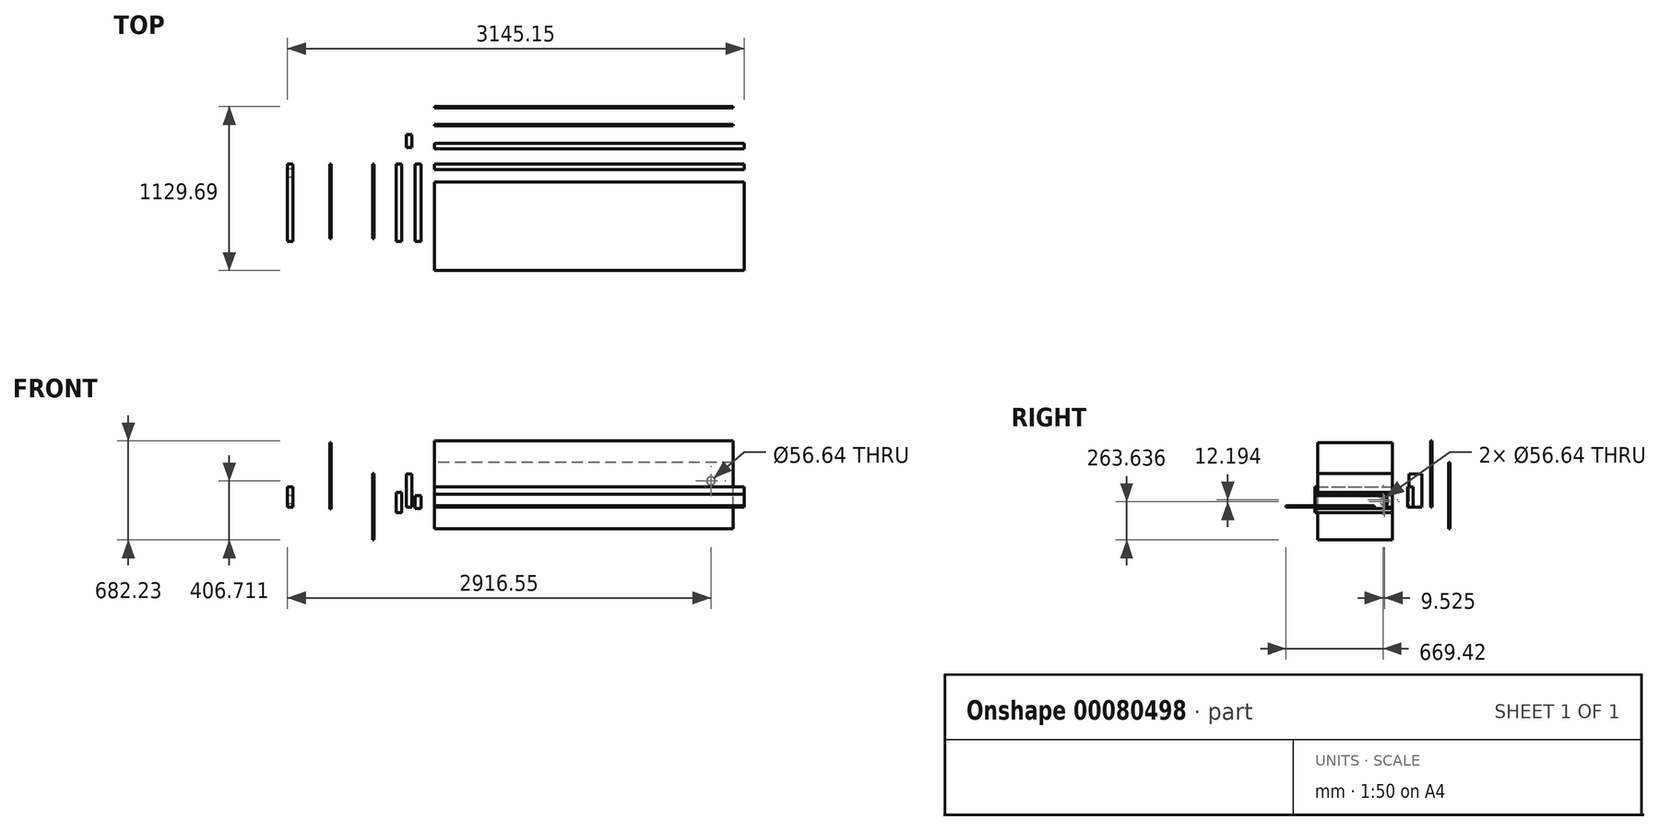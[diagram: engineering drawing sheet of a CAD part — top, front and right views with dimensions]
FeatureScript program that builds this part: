
annotation { "Feature Type Name" : "Feature", "Feature Type Description" : "" }
export const myFeature = defineFeature(function(context is Context, id is Id, definition is map)
    precondition{}
    {
        {
            var Q0;
            Q0=qCreatedBy(makeId("Right.planeOp"),FACE);
            var sketch = newSketch(context, id + "F0", { "sketchPlane" : qUnion([Q0])});
            skLineSegment(sketch, "E0.bottom", {"start": v(0, 0) * mm, "end": v(-38.1, 0) * mm});
            skLineSegment(sketch, "E0.top", {"start": v(0, 88.9) * mm, "end": v(-38.1, 88.9) * mm});
            skLineSegment(sketch, "E0.left", {"start": v(0, 0) * mm, "end": v(0, 88.9) * mm});
            skLineSegment(sketch, "E0.right", {"start": v(-38.1, 0) * mm, "end": v(-38.1, 88.9) * mm});
            skSolve(sketch);
        }
        {
            var Q0;
            Q0=makeQuery(id+"F0.imprint","IMPRINT",FACE,{"disambiguationData":[TD([[makeQuery(id+"F0.imprint","IMPRINT",EDGE,{"derivedFrom":sQuery(id+"F0.wireOp",EDGE,"E0.bottom")}),-1.0]])]});
            extrude(context, id + "F1", {"entities" : qUnion([Q0]), "depth" : 2133.6 * mm});
        }
        {
            var Q0;
            Q0=qCreatedBy(makeId("Front.planeOp"),FACE);
            var sketch = newSketch(context, id + "F2", { "sketchPlane" : qUnion([Q0])});
            skLineSegment(sketch, "E1.bottom", {"start": v(-92.86, -7.97) * mm, "end": v(-130.96, -7.97) * mm});
            skLineSegment(sketch, "E1.top", {"start": v(-92.86, 80.93) * mm, "end": v(-130.96, 80.93) * mm});
            skLineSegment(sketch, "E1.left", {"start": v(-92.86, -7.97) * mm, "end": v(-92.86, 80.93) * mm});
            skLineSegment(sketch, "E1.right", {"start": v(-130.96, -7.97) * mm, "end": v(-130.96, 80.93) * mm});
            skSolve(sketch);
        }
        {
            var Q0;
            Q0=makeQuery(id+"F2.imprint","IMPRINT",FACE,{"disambiguationData":[TD([[makeQuery(id+"F2.imprint","IMPRINT",EDGE,{"derivedFrom":sQuery(id+"F2.wireOp",EDGE,"E1.bottom")}),-1.0]])]});
            extrude(context, id + "F3", {"entities" : qUnion([Q0]), "depth" : 533.4 * mm});
        }
        {
            var Q0;
            Q0=qCreatedBy(makeId("Right.planeOp"),FACE);
            var sketch = newSketch(context, id + "F4", { "sketchPlane" : qUnion([Q0])});
            skLineSegment(sketch, "E2.bottom", {"start": v(105.82, 0) * mm, "end": v(143.92, 0) * mm});
            skLineSegment(sketch, "E2.top", {"start": v(105.82, 139.7) * mm, "end": v(143.92, 139.7) * mm});
            skLineSegment(sketch, "E2.left", {"start": v(105.82, 0) * mm, "end": v(105.82, 139.7) * mm});
            skLineSegment(sketch, "E2.right", {"start": v(143.92, 0) * mm, "end": v(143.92, 139.7) * mm});
            skSolve(sketch);
        }
        {
            var Q0;
            Q0=makeQuery(id+"F4.imprint","IMPRINT",FACE,{"disambiguationData":[TD([[makeQuery(id+"F4.imprint","IMPRINT",EDGE,{"derivedFrom":sQuery(id+"F4.wireOp",EDGE,"E2.bottom")}),1.0]])]});
            extrude(context, id + "F5", {"entities" : qUnion([Q0]), "depth" : 2133.6 * mm});
        }
        {
            var Q0;
            Q0=qCreatedBy(makeId("Front.planeOp"),FACE);
            var sketch = newSketch(context, id + "F6", { "sketchPlane" : qUnion([Q0])});
            skLineSegment(sketch, "E3.bottom", {"start": v(-225.29, -37.86) * mm, "end": v(-263.39, -37.86) * mm});
            skLineSegment(sketch, "E3.top", {"start": v(-225.29, 101.84) * mm, "end": v(-263.39, 101.84) * mm});
            skLineSegment(sketch, "E3.left", {"start": v(-225.29, -37.86) * mm, "end": v(-225.29, 101.84) * mm});
            skLineSegment(sketch, "E3.right", {"start": v(-263.39, -37.86) * mm, "end": v(-263.39, 101.84) * mm});
            skSolve(sketch);
        }
        {
            var Q0;
            Q0=makeQuery(id+"F6.imprint","IMPRINT",FACE,{"disambiguationData":[TD([[makeQuery(id+"F6.imprint","IMPRINT",EDGE,{"derivedFrom":sQuery(id+"F6.wireOp",EDGE,"E3.bottom")}),-1.0]])]});
            extrude(context, id + "F7", {"entities" : qUnion([Q0]), "depth" : 533.4 * mm});
        }
        {
            var Q0;
            Q0=qCreatedBy(makeId("Top.planeOp"),FACE);
            var sketch = newSketch(context, id + "F8", { "sketchPlane" : qUnion([Q0])});
            skLineSegment(sketch, "E4.bottom", {"start": v(-155.43, 116.63) * mm, "end": v(-193.53, 116.63) * mm});
            skLineSegment(sketch, "E4.top", {"start": v(-155.43, 205.53) * mm, "end": v(-193.53, 205.53) * mm});
            skLineSegment(sketch, "E4.left", {"start": v(-155.43, 116.63) * mm, "end": v(-155.43, 205.53) * mm});
            skLineSegment(sketch, "E4.right", {"start": v(-193.53, 116.63) * mm, "end": v(-193.53, 205.53) * mm});
            skSolve(sketch);
        }
        {
            var Q0;
            Q0=makeQuery(id+"F8.imprint","IMPRINT",FACE,{"disambiguationData":[TD([[makeQuery(id+"F8.imprint","IMPRINT",EDGE,{"derivedFrom":sQuery(id+"F8.wireOp",EDGE,"E4.bottom")}),-1.0]])]});
            extrude(context, id + "F9", {"entities" : qUnion([Q0]), "depth" : 228.6 * mm});
        }
        {
            var Q0;
            Q0=qCreatedBy(makeId("Top.planeOp"),FACE);
            var sketch = newSketch(context, id + "F10", { "sketchPlane" : qUnion([Q0])});
            skLineSegment(sketch, "E5.bottom", {"start": v(0, -123.32) * mm, "end": v(2133.6, -123.32) * mm});
            skLineSegment(sketch, "E5.top", {"start": v(0, -732.92) * mm, "end": v(2133.6, -732.92) * mm});
            skLineSegment(sketch, "E5.left", {"start": v(0, -123.32) * mm, "end": v(0, -732.92) * mm});
            skLineSegment(sketch, "E5.right", {"start": v(2133.6, -123.32) * mm, "end": v(2133.6, -732.92) * mm});
            skSolve(sketch);
        }
        {
            var Q0;
            Q0=makeQuery(id+"F10.imprint","IMPRINT",FACE,{"disambiguationData":[TD([[makeQuery(id+"F10.imprint","IMPRINT",EDGE,{"derivedFrom":sQuery(id+"F10.wireOp",EDGE,"E5.bottom")}),-1.0]])]});
            extrude(context, id + "F11", {"entities" : qUnion([Q0]), "depth" : 9.52 * mm});
        }
        {
            var Q0;
            Q0=qCreatedBy(makeId("Right.planeOp"),FACE);
            var sketch = newSketch(context, id + "F12", { "sketchPlane" : qUnion([Q0])});
            skLineSegment(sketch, "E6.bottom", {"start": v(263.25, 0) * mm, "end": v(272.78, 0) * mm});
            skLineSegment(sketch, "E6.top", {"start": v(263.25, 457.2) * mm, "end": v(272.78, 457.2) * mm});
            skLineSegment(sketch, "E6.left", {"start": v(263.25, 0) * mm, "end": v(263.25, 457.2) * mm});
            skLineSegment(sketch, "E6.right", {"start": v(272.78, 0) * mm, "end": v(272.78, 457.2) * mm});
            skSolve(sketch);
        }
        {
            var Q0;
            Q0=makeQuery(id+"F12.imprint","IMPRINT",FACE,{"disambiguationData":[TD([[makeQuery(id+"F12.imprint","IMPRINT",EDGE,{"derivedFrom":sQuery(id+"F12.wireOp",EDGE,"E6.bottom")}),1.0]])]});
            extrude(context, id + "F13", {"entities" : qUnion([Q0]), "depth" : 2057.4 * mm});
        }
        {
            var Q0;
            Q0=qCreatedBy(makeId("Right.planeOp"),FACE);
            var sketch = newSketch(context, id + "F14", { "sketchPlane" : qUnion([Q0])});
            skLineSegment(sketch, "E7.bottom", {"start": v(387.25, -148.52) * mm, "end": v(396.77, -148.52) * mm});
            skLineSegment(sketch, "E7.top", {"start": v(387.25, 308.68) * mm, "end": v(396.77, 308.68) * mm});
            skLineSegment(sketch, "E7.left", {"start": v(387.25, -148.52) * mm, "end": v(387.25, 308.68) * mm});
            skLineSegment(sketch, "E7.right", {"start": v(396.77, -148.52) * mm, "end": v(396.77, 308.68) * mm});
            skSolve(sketch);
        }
        {
            var Q0;
            Q0=makeQuery(id+"F14.imprint","IMPRINT",FACE,{"disambiguationData":[TD([[makeQuery(id+"F14.imprint","IMPRINT",EDGE,{"derivedFrom":sQuery(id+"F14.wireOp",EDGE,"E7.bottom")}),1.0]])]});
            extrude(context, id + "F15", {"entities" : qUnion([Q0]), "depth" : 2057.4 * mm});
        }
        {
            var Q0;
            Q0=qCreatedBy(makeId("Front.planeOp"),FACE);
            var sketch = newSketch(context, id + "F16", { "sketchPlane" : qUnion([Q0])});
            skLineSegment(sketch, "E8.bottom", {"start": v(-425.21, -225.03) * mm, "end": v(-415.69, -225.03) * mm});
            skLineSegment(sketch, "E8.top", {"start": v(-425.21, 232.17) * mm, "end": v(-415.69, 232.17) * mm});
            skLineSegment(sketch, "E8.left", {"start": v(-425.21, -225.03) * mm, "end": v(-425.21, 232.17) * mm});
            skLineSegment(sketch, "E8.right", {"start": v(-415.69, -225.03) * mm, "end": v(-415.69, 232.17) * mm});
            skSolve(sketch);
        }
        {
            var Q0;
            Q0=makeQuery(id+"F16.imprint","IMPRINT",FACE,{"disambiguationData":[TD([[makeQuery(id+"F16.imprint","IMPRINT",EDGE,{"derivedFrom":sQuery(id+"F16.wireOp",EDGE,"E8.bottom")}),1.0]])]});
            extrude(context, id + "F17", {"entities" : qUnion([Q0]), "depth" : 514.35 * mm});
        }
        {
            var Q0;
            Q0=qCreatedBy(makeId("Front.planeOp"),FACE);
            var sketch = newSketch(context, id + "F18", { "sketchPlane" : qUnion([Q0])});
            skLineSegment(sketch, "E9.bottom", {"start": v(-718.56, -12.2) * mm, "end": v(-709.04, -12.2) * mm});
            skLineSegment(sketch, "E9.top", {"start": v(-718.56, 445) * mm, "end": v(-709.04, 445) * mm});
            skLineSegment(sketch, "E9.left", {"start": v(-718.56, -12.2) * mm, "end": v(-718.56, 445) * mm});
            skLineSegment(sketch, "E9.right", {"start": v(-709.04, -12.2) * mm, "end": v(-709.04, 445) * mm});
            skSolve(sketch);
        }
        {
            var Q0;
            Q0=makeQuery(id+"F18.imprint","IMPRINT",FACE,{"disambiguationData":[TD([[makeQuery(id+"F18.imprint","IMPRINT",EDGE,{"derivedFrom":sQuery(id+"F18.wireOp",EDGE,"E9.bottom")}),1.0]])]});
            extrude(context, id + "F19", {"entities" : qUnion([Q0]), "depth" : 514.35 * mm});
        }
        {
            var Q0;
            Q0=qCreatedBy(makeId("Front.planeOp"),FACE);
            var sketch = newSketch(context, id + "F20", { "sketchPlane" : qUnion([Q0])});
            skLineSegment(sketch, "E10.bottom", {"start": v(-973.45, 0) * mm, "end": v(-1011.55, 0) * mm});
            skLineSegment(sketch, "E10.top", {"start": v(-973.45, 139.7) * mm, "end": v(-1011.55, 139.7) * mm});
            skLineSegment(sketch, "E10.left", {"start": v(-973.45, 0) * mm, "end": v(-973.45, 139.7) * mm});
            skLineSegment(sketch, "E10.right", {"start": v(-1011.55, 0) * mm, "end": v(-1011.55, 139.7) * mm});
            skSolve(sketch);
        }
        {
            var Q0;
            Q0=makeQuery(id+"F20.imprint","IMPRINT",FACE,{"disambiguationData":[TD([[makeQuery(id+"F20.imprint","IMPRINT",EDGE,{"derivedFrom":sQuery(id+"F20.wireOp",EDGE,"E10.bottom")}),-1.0]])]});
            extrude(context, id + "F21", {"entities" : qUnion([Q0]), "depth" : 533.4 * mm});
        }
        {
            var Q0;
            Q0=makeQuery(id+"F21.opExtrude","SWEPT_FACE",FACE,{"disambiguationData":[OSD([sQuery(id+"F20.wireOp",EDGE,"E10.right")])]});
            var sketch = newSketch(context, id + "F22", { "sketchPlane" : qUnion([Q0])});
            skCircle(sketch, "E11", {"center": v(63.5, 50.8) * mm, "radius": 28.32 * mm});
            skSolve(sketch);
        }
        {
            var Q0;
            Q0=makeQuery(id+"F22.imprint","IMPRINT",FACE,{"disambiguationData":[TD([[makeQuery(id+"F22.imprint","IMPRINT",EDGE,{"derivedFrom":sQuery(id+"F22.wireOp",EDGE,"E11")}),1.0]])]});
            extrude(context, id + "F23", {"entities" : qUnion([Q0]), "operationType" : NewBodyOperationType.REMOVE, "oppositeDirection" : true, "depth" : 38.1 * mm});
        }
        {
            var Q0;
            Q0=makeQuery(id+"F19.opExtrude","SWEPT_FACE",FACE,{"disambiguationData":[OSD([sQuery(id+"F18.wireOp",EDGE,"E9.left")])]});
            var sketch = newSketch(context, id + "F24", { "sketchPlane" : qUnion([Q0])});
            skCircle(sketch, "E12", {"center": v(53.98, 38.6) * mm, "radius": 28.32 * mm});
            skSolve(sketch);
        }
        {
            var Q0;
            Q0=makeQuery(id+"F24.imprint","IMPRINT",FACE,{"disambiguationData":[TD([[makeQuery(id+"F24.imprint","IMPRINT",EDGE,{"derivedFrom":sQuery(id+"F24.wireOp",EDGE,"E12")}),1.0]])]});
            extrude(context, id + "F25", {"entities" : qUnion([Q0]), "operationType" : NewBodyOperationType.REMOVE, "oppositeDirection" : true, "depth" : 9.52 * mm});
        }
        {
            var Q0;
            Q0=makeQuery(id+"F15.opExtrude","SWEPT_FACE",FACE,{"disambiguationData":[OSD([sQuery(id+"F14.wireOp",EDGE,"E7.right")])]});
            var sketch = newSketch(context, id + "F26", { "sketchPlane" : qUnion([Q0])});
            skCircle(sketch, "E13", {"center": v(-1905, 181.68) * mm, "radius": 28.32 * mm});
            skSolve(sketch);
        }
        {
            var Q0;
            Q0=makeQuery(id+"F26.imprint","IMPRINT",FACE,{"disambiguationData":[TD([[makeQuery(id+"F26.imprint","IMPRINT",EDGE,{"derivedFrom":sQuery(id+"F26.wireOp",EDGE,"E13")}),1.0]])]});
            extrude(context, id + "F27", {"entities" : qUnion([Q0]), "operationType" : NewBodyOperationType.REMOVE, "oppositeDirection" : true, "depth" : 25.4 * mm});
        }
    });
